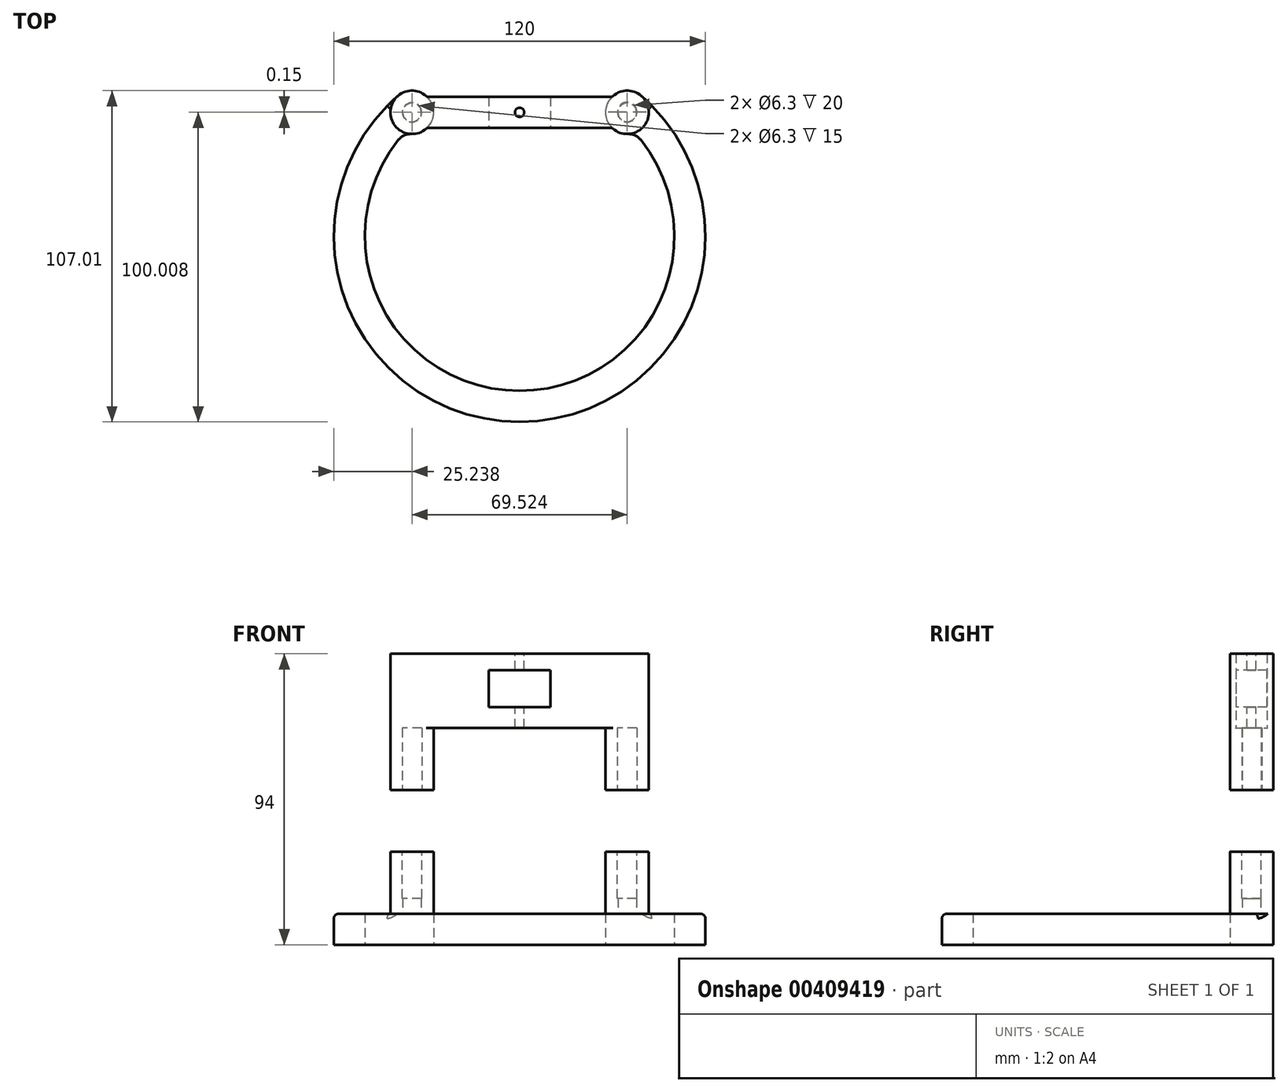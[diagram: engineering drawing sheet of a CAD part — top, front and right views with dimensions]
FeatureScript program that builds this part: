
annotation { "Feature Type Name" : "Feature", "Feature Type Description" : "" }
export const myFeature = defineFeature(function(context is Context, id is Id, definition is map)
    precondition{}
    {
        {
            var Q0;
            Q0=qCreatedBy(makeId("Top.planeOp"),FACE);
            var sketch = newSketch(context, id + "F0", { "sketchPlane" : qUnion([Q0])});
            skArc(sketch, "E0", {"start": v(-39.35, 45.3) * mm, "mid": v(0, -60) * mm, "end": v(39.35, 45.3) * mm});
            skLineSegment(sketch, "E1", {"start": v(-53.56, 40) * mm, "end": v(68.3, 40) * mm, "construction": true});
            skArc(sketch, "E2", {"start": v(-35.03, 33.01) * mm, "mid": v(-28.16, 42.33) * mm, "end": v(-39.35, 45.3) * mm});
            skArc(sketch, "E3", {"start": v(39.35, 45.3) * mm, "mid": v(28.16, 42.33) * mm, "end": v(35.03, 33.01) * mm});
            skArc(sketch, "E4.trimOffspring", {"start": v(-39.13, 31.13) * mm, "mid": v(0, -50) * mm, "end": v(39.13, 31.13) * mm});
            skPoint(sketch, "E5.visualSharp", {"position": v(-37.17, 33.44) * mm});
            skArc(sketch, "E5.filletArc", {"start": v(-35.03, 33.01) * mm, "mid": v(-37.3, 32.56) * mm, "end": v(-39.13, 31.13) * mm});
            skPoint(sketch, "E6.visualSharp", {"position": v(37.17, 33.44) * mm});
            skArc(sketch, "E6.filletArc", {"start": v(39.13, 31.13) * mm, "mid": v(37.3, 32.56) * mm, "end": v(35.03, 33.01) * mm});
            skSolve(sketch);
        }
        {
            var Q0;
            Q0 = qSketchRegion(id + "F0", true);
            extrude(context, id + "F1", {"entities" : qUnion([Q0]), "depth" : 10 * mm, "offsetDistance" : 25 * mm});
        }
        {
            var Q0;
            Q0=makeQuery(id+"F1.opExtrude","CAP_FACE",FACE,{"disambiguationData":[OSD([sQuery(id+"F0.wireOp",EDGE,"E0"),sQuery(id+"F0.wireOp",EDGE,"E2"),sQuery(id+"F0.wireOp",EDGE,"E3"),sQuery(id+"F0.wireOp",EDGE,"E4.trimOffspring"),sQuery(id+"F0.wireOp",EDGE,"E5.filletArc"),sQuery(id+"F0.wireOp",EDGE,"E6.filletArc")])],"isStart":false});
            var sketch = newSketch(context, id + "F2", { "sketchPlane" : qUnion([Q0])});
            skCircle(sketch, "E7", {"center": v(-34.76, 40) * mm, "radius": 3 * mm});
            skCircle(sketch, "E8", {"center": v(-34.76, 40) * mm, "radius": 7 * mm});
            skCircle(sketch, "E9", {"center": v(34.76, 40) * mm, "radius": 7 * mm});
            skCircle(sketch, "E10", {"center": v(34.76, 40) * mm, "radius": 3 * mm});
            skSolve(sketch);
        }
        {
            var Q0;
            Q0 = qSketchRegion(id + "F2", true);
            extrude(context, id + "F3", {"entities" : qUnion([Q0]), "operationType" : NewBodyOperationType.ADD, "depth" : 20 * mm, "offsetDistance" : 25 * mm});
        }
        {
            var Q0;
            Q0=makeQuery(id+"F3.opExtrude","CAP_FACE",FACE,{"disambiguationData":[OSD([sQuery(id+"F2.wireOp",EDGE,"E7"),sQuery(id+"F2.wireOp",EDGE,"E8")])],"isStart":false});
            var sketch = newSketch(context, id + "F4", { "sketchPlane" : qUnion([Q0])});
            skCircle(sketch, "E11", {"center": v(-34.76, 40) * mm, "radius": 3.15 * mm});
            skCircle(sketch, "E12", {"center": v(34.76, 40) * mm, "radius": 3.15 * mm});
            skSolve(sketch);
        }
        {
            var Q0;
            Q0 = qSketchRegion(id + "F4", true);
            extrude(context, id + "F5", {"entities" : qUnion([Q0]), "operationType" : NewBodyOperationType.REMOVE, "oppositeDirection" : true, "depth" : 15 * mm, "offsetDistance" : 25 * mm});
        }
        {
            var Q0;
            Q0=makeQuery(id+"F1.opExtrude","CAP_EDGE",EDGE,{"disambiguationData":[OSD([sQuery(id+"F0.wireOp",EDGE,"E0")])],"isStart":false});
            fillet(context, id + "F6", {"entities" : qUnion([Q0]), "radius" : 1.5 * mm, "tangentPropagation" : true, "allowEdgeOverflow" : false});
        }
        {
            var Q0;
            Q0=qCreatedBy(makeId("Top.planeOp"),FACE);
            cPlane(context, id + "F7", {"entities" : qUnion([Q0]), "cplaneType" : CPlaneType.OFFSET, "offset" : 50 * mm, "width" : 150 * mm, "height" : 150 * mm});
        }
        {
            var Q0;
            Q0=qCreatedBy(id+"F7.planeOp",FACE);
            var sketch = newSketch(context, id + "F8", { "sketchPlane" : qUnion([Q0])});
            skCircle(sketch, "E13.0", {"center": v(-34.76, 40) * mm, "radius": 7 * mm});
            skCircle(sketch, "E14.0", {"center": v(-34.76, 40) * mm, "radius": 3.15 * mm});
            skCircle(sketch, "E15.0", {"center": v(34.76, 40) * mm, "radius": 7 * mm});
            skCircle(sketch, "E16.0", {"center": v(34.76, 40.16) * mm, "radius": 3.15 * mm});
            skSolve(sketch);
        }
        {
            var Q0;
            Q0 = qSketchRegion(id + "F8", true);
            extrude(context, id + "F9", {"entities" : qUnion([Q0]), "depth" : 20 * mm, "offsetDistance" : 25 * mm});
        }
        {
            var Q0;
            Q0=makeQuery(id+"F9.opExtrude","CAP_FACE",FACE,{"disambiguationData":[OSD([sQuery(id+"F8.wireOp",EDGE,"E13.0"),sQuery(id+"F8.wireOp",EDGE,"E14.0")])],"isStart":false});
            var sketch = newSketch(context, id + "F10", { "sketchPlane" : qUnion([Q0])});
            skArc(sketch, "E17", {"start": v(-30.13, 45.26) * mm, "mid": v(-41.76, 40) * mm, "end": v(-30.13, 34.76) * mm});
            skArc(sketch, "E18", {"start": v(30.13, 34.76) * mm, "mid": v(41.76, 40) * mm, "end": v(30.13, 45.26) * mm});
            skLineSegment(sketch, "E19", {"start": v(-34.76, 40) * mm, "end": v(34.76, 40) * mm, "construction": true});
            skLineSegment(sketch, "E20", {"start": v(-29.47, 45) * mm, "end": v(29.47, 45) * mm});
            skLineSegment(sketch, "E21", {"start": v(-29.47, 35) * mm, "end": v(29.47, 35) * mm});
            skPoint(sketch, "E22.orphan", {"position": v(-34.76, 45) * mm});
            skPoint(sketch, "E23.orphan", {"position": v(34.35, 35) * mm});
            skPoint(sketch, "E24.orphan", {"position": v(34.35, 45) * mm});
            skPoint(sketch, "E25.visualSharp", {"position": v(-29.86, 45) * mm});
            skArc(sketch, "E25.filletArc", {"start": v(-30.13, 45.26) * mm, "mid": v(-29.82, 45.07) * mm, "end": v(-29.47, 45) * mm});
            skPoint(sketch, "E26.visualSharp", {"position": v(29.86, 45) * mm});
            skArc(sketch, "E26.filletArc", {"start": v(29.47, 45) * mm, "mid": v(29.82, 45.07) * mm, "end": v(30.13, 45.26) * mm});
            skPoint(sketch, "E27.visualSharp", {"position": v(29.86, 35) * mm});
            skArc(sketch, "E27.filletArc", {"start": v(30.13, 34.76) * mm, "mid": v(29.82, 34.94) * mm, "end": v(29.47, 35) * mm});
            skPoint(sketch, "E28.visualSharp", {"position": v(-29.86, 35) * mm});
            skArc(sketch, "E28.filletArc", {"start": v(-29.47, 35) * mm, "mid": v(-29.82, 34.94) * mm, "end": v(-30.13, 34.76) * mm});
            skSolve(sketch);
        }
        {
            var Q0;
            Q0 = qSketchRegion(id + "F10", true);
            extrude(context, id + "F11", {"entities" : qUnion([Q0]), "operationType" : NewBodyOperationType.ADD, "depth" : 24 * mm, "offsetDistance" : 25 * mm});
        }
        {
            var Q0;
            Q0=makeQuery(id+"F11.opExtrude","SWEPT_FACE",FACE,{"disambiguationData":[OSD([sQuery(id+"F10.wireOp",EDGE,"E21")])]});
            var sketch = newSketch(context, id + "F12", { "sketchPlane" : qUnion([Q0])});
            skLineSegment(sketch, "E29", {"start": v(0, 0) * mm, "end": v(0, 112.59) * mm, "construction": true});
            skLineSegment(sketch, "E30.bottom", {"start": v(10, 88.75) * mm, "end": v(-10, 88.75) * mm});
            skLineSegment(sketch, "E30.top", {"start": v(10, 76.75) * mm, "end": v(-10, 76.75) * mm});
            skLineSegment(sketch, "E30.left", {"start": v(10, 88.75) * mm, "end": v(10, 76.75) * mm});
            skLineSegment(sketch, "E30.right", {"start": v(-10, 88.75) * mm, "end": v(-10, 76.75) * mm});
            skPoint(sketch, "E30.middle", {"position": v(0, 82.75) * mm});
            skSolve(sketch);
        }
        {
            var Q0;
            Q0 = qSketchRegion(id + "F12", true);
            extrude(context, id + "F13", {"entities" : qUnion([Q0]), "operationType" : NewBodyOperationType.REMOVE, "endBound" : BoundingType.THROUGH_ALL, "oppositeDirection" : true, "depth" : 25 * mm, "offsetDistance" : 25 * mm});
        }
        {
            var Q0;
            Q0=makeQuery(id+"F11.opExtrude","CAP_FACE",FACE,{"disambiguationData":[OSD([sQuery(id+"F10.wireOp",EDGE,"E17"),sQuery(id+"F10.wireOp",EDGE,"E18"),sQuery(id+"F10.wireOp",EDGE,"E20"),sQuery(id+"F10.wireOp",EDGE,"E21"),sQuery(id+"F10.wireOp",EDGE,"E25.filletArc"),sQuery(id+"F10.wireOp",EDGE,"E26.filletArc"),sQuery(id+"F10.wireOp",EDGE,"E27.filletArc"),sQuery(id+"F10.wireOp",EDGE,"E28.filletArc")])],"isStart":false});
            var sketch = newSketch(context, id + "F14", { "sketchPlane" : qUnion([Q0])});
            skLineSegment(sketch, "E31", {"start": v(0, 0) * mm, "end": v(0, 56.22) * mm, "construction": true});
            skCircle(sketch, "E32", {"center": v(0, 40) * mm, "radius": 1.5 * mm});
            skSolve(sketch);
        }
        {
            var Q0;
            Q0 = qSketchRegion(id + "F14", true);
            extrude(context, id + "F15", {"entities" : qUnion([Q0]), "operationType" : NewBodyOperationType.REMOVE, "oppositeDirection" : true, "depth" : 25 * mm, "offsetDistance" : 25 * mm});
        }
    });
